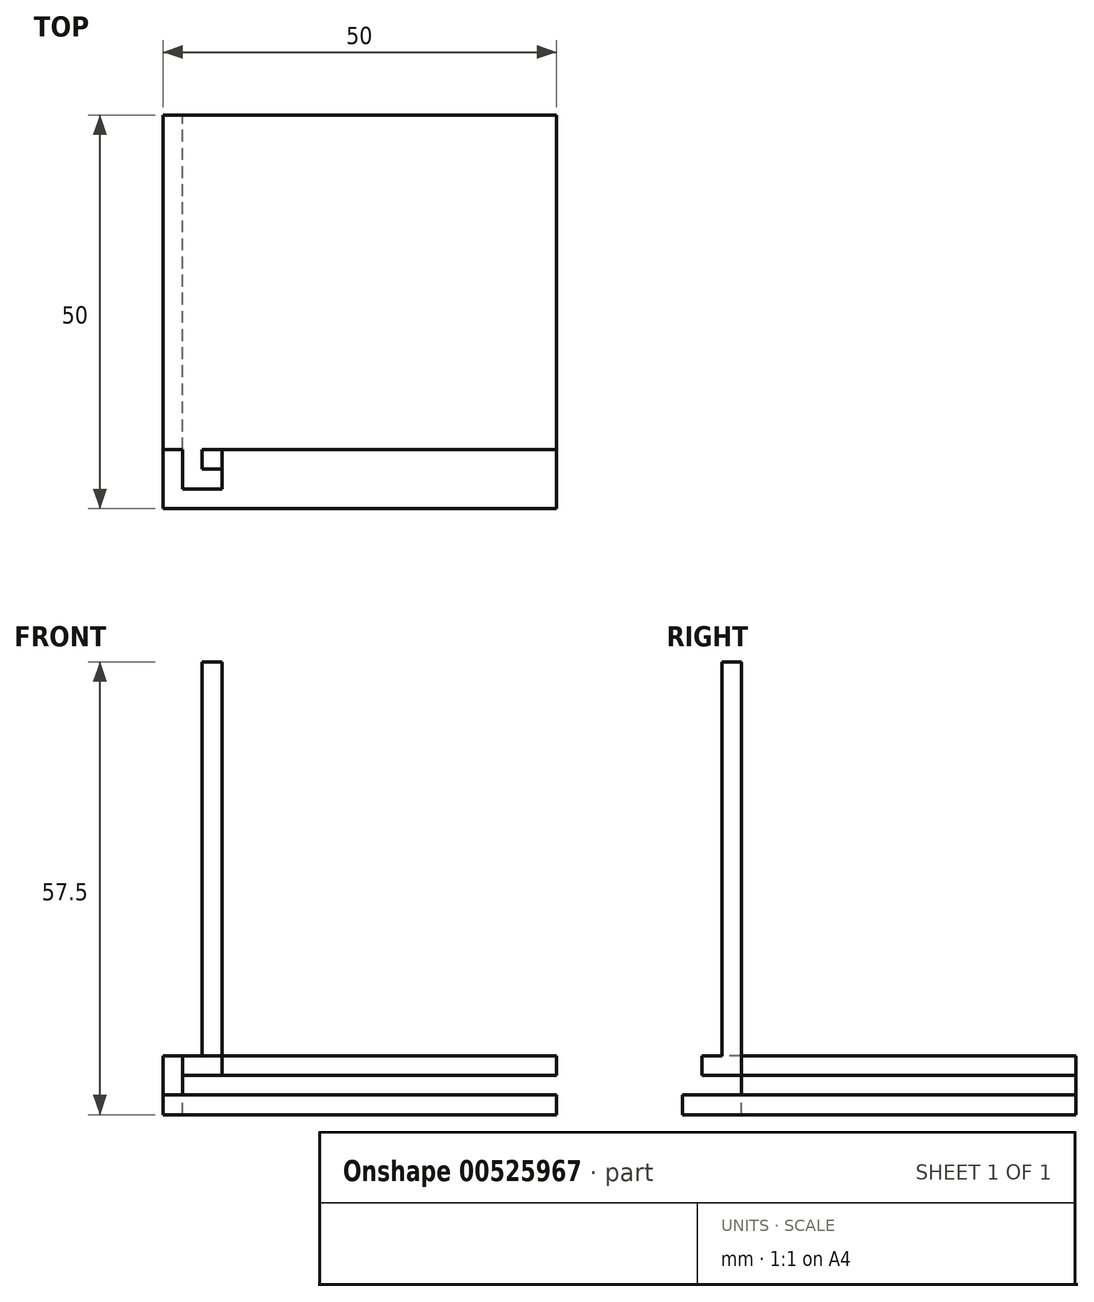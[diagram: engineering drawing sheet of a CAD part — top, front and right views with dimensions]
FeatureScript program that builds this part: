
annotation { "Feature Type Name" : "Feature", "Feature Type Description" : "" }
export const myFeature = defineFeature(function(context is Context, id is Id, definition is map)
    precondition{}
    {
        {
            var Q0;
            Q0=qCreatedBy(makeId("Top.planeOp"),FACE);
            var sketch = newSketch(context, id + "F0", { "sketchPlane" : qUnion([Q0])});
            skLineSegment(sketch, "E0.bottom", {"start": v(-21.7, 29.61) * mm, "end": v(28.3, 29.61) * mm});
            skLineSegment(sketch, "E0.top", {"start": v(-21.7, -20.39) * mm, "end": v(28.3, -20.39) * mm});
            skLineSegment(sketch, "E0.left", {"start": v(-21.7, 29.61) * mm, "end": v(-21.7, -20.39) * mm});
            skLineSegment(sketch, "E0.right", {"start": v(28.3, 29.61) * mm, "end": v(28.3, -20.39) * mm});
            skLineSegment(sketch, "E1.bottom", {"start": v(-21.7, 29.61) * mm, "end": v(-19.2, 29.61) * mm});
            skLineSegment(sketch, "E1.top", {"start": v(-21.7, -20.39) * mm, "end": v(-19.2, -20.39) * mm});
            skLineSegment(sketch, "E1.right", {"start": v(-19.2, 29.61) * mm, "end": v(-19.2, -20.39) * mm});
            skLineSegment(sketch, "E2.top", {"start": v(-21.7, -17.89) * mm, "end": v(28.3, -17.89) * mm});
            skLineSegment(sketch, "E2.left", {"start": v(-21.7, -20.39) * mm, "end": v(-21.7, -17.89) * mm});
            skLineSegment(sketch, "E2.right", {"start": v(28.3, -20.39) * mm, "end": v(28.3, -17.89) * mm});
            skLineSegment(sketch, "E3.bottom", {"start": v(-19.2, 29.61) * mm, "end": v(-16.7, 29.61) * mm});
            skLineSegment(sketch, "E3.top", {"start": v(-19.2, -20.39) * mm, "end": v(-16.7, -20.39) * mm});
            skLineSegment(sketch, "E3.right", {"start": v(-16.7, 29.61) * mm, "end": v(-16.7, -20.39) * mm});
            skLineSegment(sketch, "E4.bottom", {"start": v(-16.7, 29.61) * mm, "end": v(-14.2, 29.61) * mm});
            skLineSegment(sketch, "E4.top", {"start": v(-16.7, -20.39) * mm, "end": v(-14.2, -20.39) * mm});
            skLineSegment(sketch, "E4.right", {"start": v(-14.2, 29.61) * mm, "end": v(-14.2, -20.39) * mm});
            skLineSegment(sketch, "E5.top", {"start": v(-21.7, -15.39) * mm, "end": v(28.3, -15.39) * mm});
            skLineSegment(sketch, "E5.left", {"start": v(-21.7, -17.89) * mm, "end": v(-21.7, -15.39) * mm});
            skLineSegment(sketch, "E5.right", {"start": v(28.3, -17.89) * mm, "end": v(28.3, -15.39) * mm});
            skLineSegment(sketch, "E6.top", {"start": v(-21.7, -12.89) * mm, "end": v(28.3, -12.89) * mm});
            skLineSegment(sketch, "E6.left", {"start": v(-21.7, -15.39) * mm, "end": v(-21.7, -12.89) * mm});
            skLineSegment(sketch, "E6.right", {"start": v(28.3, -15.39) * mm, "end": v(28.3, -12.89) * mm});
            skSolve(sketch);
        }
        {
            var Q0;
            {var subQ0=sQuery(id+"F0.wireOp",EDGE,"E0.bottom");Q0=makeQuery(id+"F0.imprint","IMPRINT",FACE,{"disambiguationData":[TD([[makeQuery(id+"F0.imprint","IMPRINT",EDGE,{"derivedFrom":subQ0}),-1.0]])]});}
            var Q1;
            {var subQ0=sQuery(id+"F0.wireOp",EDGE,"E4.bottom");Q1=makeQuery(id+"F0.imprint","IMPRINT",FACE,{"disambiguationData":[TD([[makeQuery(id+"F0.imprint","IMPRINT",EDGE,{"derivedFrom":subQ0}),-1.0]])]});}
            var Q2;
            {var subQ0=sQuery(id+"F0.wireOp",EDGE,"E3.bottom");Q2=makeQuery(id+"F0.imprint","IMPRINT",FACE,{"disambiguationData":[TD([[makeQuery(id+"F0.imprint","IMPRINT",EDGE,{"derivedFrom":subQ0}),-1.0]])]});}
            var Q3;
            {var subQ0=sQuery(id+"F0.wireOp",EDGE,"E1.bottom");Q3=makeQuery(id+"F0.imprint","IMPRINT",FACE,{"disambiguationData":[TD([[makeQuery(id+"F0.imprint","IMPRINT",EDGE,{"derivedFrom":subQ0}),-1.0]])]});}
            var Q4;
            {var subQ5=sQuery(id+"F0.wireOp",EDGE,"E6.right");Q4=makeQuery(id+"F0.imprint","IMPRINT",FACE,{"disambiguationData":[TD([[makeQuery(id+"F0.imprint","IMPRINT",EDGE,{"derivedFrom":subQ5}),1.0]])]});}
            var Q5;
            {var subQ5=sQuery(id+"F0.wireOp",EDGE,"E5.right");Q5=makeQuery(id+"F0.imprint","IMPRINT",FACE,{"disambiguationData":[TD([[makeQuery(id+"F0.imprint","IMPRINT",EDGE,{"derivedFrom":subQ5}),1.0]])]});}
            var Q6;
            {var subQ0=sQuery(id+"F0.wireOp",EDGE,"E2.right");Q6=makeQuery(id+"F0.imprint","IMPRINT",FACE,{"disambiguationData":[TD([[makeQuery(id+"F0.imprint","IMPRINT",EDGE,{"derivedFrom":subQ0}),1.0]])]});}
            var Q7;
            {var subQ0=sQuery(id+"F0.wireOp",EDGE,"E4.top");Q7=makeQuery(id+"F0.imprint","IMPRINT",FACE,{"disambiguationData":[TD([[makeQuery(id+"F0.imprint","IMPRINT",EDGE,{"derivedFrom":subQ0}),1.0]])]});}
            var Q8;
            {var subQ0=sQuery(id+"F0.wireOp",EDGE,"E3.top");Q8=makeQuery(id+"F0.imprint","IMPRINT",FACE,{"disambiguationData":[TD([[makeQuery(id+"F0.imprint","IMPRINT",EDGE,{"derivedFrom":subQ0}),1.0]])]});}
            var Q9;
            {var subQ0=sQuery(id+"F0.wireOp",EDGE,"E2.left");Q9=makeQuery(id+"F0.imprint","IMPRINT",FACE,{"disambiguationData":[TD([[makeQuery(id+"F0.imprint","IMPRINT",EDGE,{"derivedFrom":subQ0}),-1.0]])]});}
            var Q10;
            {var subQ5=sQuery(id+"F0.wireOp",EDGE,"E5.left");Q10=makeQuery(id+"F0.imprint","IMPRINT",FACE,{"disambiguationData":[TD([[makeQuery(id+"F0.imprint","IMPRINT",EDGE,{"derivedFrom":subQ5}),-1.0]])]});}
            var Q11;
            {var subQ0=sQuery(id+"F0.wireOp",EDGE,"E5.top");var subQ1=sQuery(id+"F0.wireOp",EDGE,"E1.right");var subQ2=makeQuery(id+"F0.imprint","INTERSECT",VERTEX,{"derivedFrom":[subQ1,subQ0]});Q11=makeQuery(id+"F0.imprint","IMPRINT",FACE,{"disambiguationData":[TD([[makeQuery(id+"F0.imprint","IMPRINT",EDGE,{"disambiguationData":[TD([[subQ2,-1.0]])],"derivedFrom":subQ1}),1.0]])]});}
            var Q12;
            {var subQ0=sQuery(id+"F0.wireOp",EDGE,"E5.top");var subQ1=sQuery(id+"F0.wireOp",EDGE,"E3.right");var subQ2=makeQuery(id+"F0.imprint","INTERSECT",VERTEX,{"derivedFrom":[subQ1,subQ0]});Q12=makeQuery(id+"F0.imprint","IMPRINT",FACE,{"disambiguationData":[TD([[makeQuery(id+"F0.imprint","IMPRINT",EDGE,{"disambiguationData":[TD([[subQ2,-1.0]])],"derivedFrom":subQ1}),1.0]])]});}
            var Q13;
            {var subQ0=sQuery(id+"F0.wireOp",EDGE,"E6.top");var subQ1=sQuery(id+"F0.wireOp",EDGE,"E3.right");var subQ2=makeQuery(id+"F0.imprint","INTERSECT",VERTEX,{"derivedFrom":[subQ1,subQ0]});Q13=makeQuery(id+"F0.imprint","IMPRINT",FACE,{"disambiguationData":[TD([[makeQuery(id+"F0.imprint","IMPRINT",EDGE,{"disambiguationData":[TD([[subQ2,-1.0]])],"derivedFrom":subQ1}),1.0]])]});}
            var Q14;
            {var subQ0=sQuery(id+"F0.wireOp",EDGE,"E6.top");var subQ1=sQuery(id+"F0.wireOp",EDGE,"E1.right");var subQ2=makeQuery(id+"F0.imprint","INTERSECT",VERTEX,{"derivedFrom":[subQ1,subQ0]});Q14=makeQuery(id+"F0.imprint","IMPRINT",FACE,{"disambiguationData":[TD([[makeQuery(id+"F0.imprint","IMPRINT",EDGE,{"disambiguationData":[TD([[subQ2,-1.0]])],"derivedFrom":subQ1}),1.0]])]});}
            var Q15;
            {var subQ5=sQuery(id+"F0.wireOp",EDGE,"E6.left");Q15=makeQuery(id+"F0.imprint","IMPRINT",FACE,{"disambiguationData":[TD([[makeQuery(id+"F0.imprint","IMPRINT",EDGE,{"derivedFrom":subQ5}),-1.0]])]});}
            extrude(context, id + "F1", {"entities" : qUnion([Q0, Q1, Q2, Q3, Q4, Q5, Q6, Q7, Q8, Q9, Q10, Q11, Q12, Q13, Q14, Q15]), "oppositeDirection" : true, "depth" : 2.5 * mm, "offsetDistance" : 25 * mm});
        }
        {
            var Q0;
            {var subQ0=sQuery(id+"F0.wireOp",EDGE,"E1.bottom");Q0=makeQuery(id+"F0.imprint","IMPRINT",FACE,{"disambiguationData":[TD([[makeQuery(id+"F0.imprint","IMPRINT",EDGE,{"derivedFrom":subQ0}),-1.0]])]});}
            var Q1;
            {var subQ5=sQuery(id+"F0.wireOp",EDGE,"E6.left");Q1=makeQuery(id+"F0.imprint","IMPRINT",FACE,{"disambiguationData":[TD([[makeQuery(id+"F0.imprint","IMPRINT",EDGE,{"derivedFrom":subQ5}),-1.0]])]});}
            var Q2;
            {var subQ0=sQuery(id+"F0.wireOp",EDGE,"E4.bottom");Q2=makeQuery(id+"F0.imprint","IMPRINT",FACE,{"disambiguationData":[TD([[makeQuery(id+"F0.imprint","IMPRINT",EDGE,{"derivedFrom":subQ0}),-1.0]])]});}
            var Q3;
            {var subQ0=sQuery(id+"F0.wireOp",EDGE,"E6.top");var subQ1=sQuery(id+"F0.wireOp",EDGE,"E3.right");var subQ2=makeQuery(id+"F0.imprint","INTERSECT",VERTEX,{"derivedFrom":[subQ1,subQ0]});Q3=makeQuery(id+"F0.imprint","IMPRINT",FACE,{"disambiguationData":[TD([[makeQuery(id+"F0.imprint","IMPRINT",EDGE,{"disambiguationData":[TD([[subQ2,-1.0]])],"derivedFrom":subQ1}),1.0]])]});}
            var Q4;
            {var subQ0=sQuery(id+"F0.wireOp",EDGE,"E4.top");Q4=makeQuery(id+"F0.imprint","IMPRINT",FACE,{"disambiguationData":[TD([[makeQuery(id+"F0.imprint","IMPRINT",EDGE,{"derivedFrom":subQ0}),1.0]])]});}
            var Q5;
            {var subQ5=sQuery(id+"F0.wireOp",EDGE,"E6.right");Q5=makeQuery(id+"F0.imprint","IMPRINT",FACE,{"disambiguationData":[TD([[makeQuery(id+"F0.imprint","IMPRINT",EDGE,{"derivedFrom":subQ5}),1.0]])]});}
            var Q6;
            {var subQ0=sQuery(id+"F0.wireOp",EDGE,"E3.top");Q6=makeQuery(id+"F0.imprint","IMPRINT",FACE,{"disambiguationData":[TD([[makeQuery(id+"F0.imprint","IMPRINT",EDGE,{"derivedFrom":subQ0}),1.0]])]});}
            var Q7;
            {var subQ0=sQuery(id+"F0.wireOp",EDGE,"E2.left");Q7=makeQuery(id+"F0.imprint","IMPRINT",FACE,{"disambiguationData":[TD([[makeQuery(id+"F0.imprint","IMPRINT",EDGE,{"derivedFrom":subQ0}),-1.0]])]});}
            var Q8;
            {var subQ0=sQuery(id+"F0.wireOp",EDGE,"E2.right");Q8=makeQuery(id+"F0.imprint","IMPRINT",FACE,{"disambiguationData":[TD([[makeQuery(id+"F0.imprint","IMPRINT",EDGE,{"derivedFrom":subQ0}),1.0]])]});}
            var Q9;
            {var subQ5=sQuery(id+"F0.wireOp",EDGE,"E5.left");Q9=makeQuery(id+"F0.imprint","IMPRINT",FACE,{"disambiguationData":[TD([[makeQuery(id+"F0.imprint","IMPRINT",EDGE,{"derivedFrom":subQ5}),-1.0]])]});}
            extrude(context, id + "F2", {"entities" : qUnion([Q0, Q1, Q2, Q3, Q4, Q5, Q6, Q7, Q8, Q9]), "operationType" : NewBodyOperationType.ADD, "depth" : 50 * mm, "offsetDistance" : 25 * mm});
        }
        {
            var Q0;
            Q0=makeQuery(id+"F1.opExtrude","CAP_FACE",FACE,{"disambiguationData":[OSD([sQuery(id+"F0.wireOp",EDGE,"E0.bottom"),sQuery(id+"F0.wireOp",EDGE,"E0.right"),sQuery(id+"F0.wireOp",EDGE,"E1.bottom"),sQuery(id+"F0.wireOp",EDGE,"E0.left"),sQuery(id+"F0.wireOp",EDGE,"E0.top"),sQuery(id+"F0.wireOp",EDGE,"E2.left"),sQuery(id+"F0.wireOp",EDGE,"E2.right"),sQuery(id+"F0.wireOp",EDGE,"E3.bottom"),sQuery(id+"F0.wireOp",EDGE,"E3.top"),sQuery(id+"F0.wireOp",EDGE,"E4.bottom"),sQuery(id+"F0.wireOp",EDGE,"E4.top"),sQuery(id+"F0.wireOp",EDGE,"E5.left"),sQuery(id+"F0.wireOp",EDGE,"E5.right"),sQuery(id+"F0.wireOp",EDGE,"E6.left"),sQuery(id+"F0.wireOp",EDGE,"E6.right")])],"isStart":false});
            var sketch = newSketch(context, id + "F3", { "sketchPlane" : qUnion([Q0])});
            skLineSegment(sketch, "E7.bottom", {"start": v(-21.7, 20.39) * mm, "end": v(-19.2, 20.39) * mm});
            skLineSegment(sketch, "E7.top", {"start": v(-21.7, -29.61) * mm, "end": v(-19.2, -29.61) * mm});
            skLineSegment(sketch, "E7.left", {"start": v(-21.7, 20.39) * mm, "end": v(-21.7, -29.61) * mm});
            skLineSegment(sketch, "E7.right", {"start": v(-19.2, 20.39) * mm, "end": v(-19.2, -29.61) * mm});
            skLineSegment(sketch, "E8.bottom", {"start": v(-21.7, 20.39) * mm, "end": v(28.3, 20.39) * mm});
            skLineSegment(sketch, "E8.top", {"start": v(-21.7, 17.89) * mm, "end": v(28.3, 17.89) * mm});
            skLineSegment(sketch, "E8.left", {"start": v(-21.7, 20.39) * mm, "end": v(-21.7, 17.89) * mm});
            skLineSegment(sketch, "E8.right", {"start": v(28.3, 20.39) * mm, "end": v(28.3, 17.89) * mm});
            skSolve(sketch);
        }
        {
            var Q0;
            {var subQ0=sQuery(id+"F3.wireOp",EDGE,"E7.top");Q0=makeQuery(id+"F3.imprint","IMPRINT",FACE,{"disambiguationData":[TD([[makeQuery(id+"F3.imprint","IMPRINT",EDGE,{"derivedFrom":subQ0}),1.0]])]});}
            var Q1;
            {var subQ5=sQuery(id+"F3.wireOp",EDGE,"E8.right");Q1=makeQuery(id+"F3.imprint","IMPRINT",FACE,{"disambiguationData":[TD([[makeQuery(id+"F3.imprint","IMPRINT",EDGE,{"derivedFrom":subQ5}),1.0]])]});}
            var Q2;
            {var subQ5=sQuery(id+"F3.wireOp",EDGE,"E8.left");Q2=makeQuery(id+"F3.imprint","IMPRINT",FACE,{"disambiguationData":[TD([[makeQuery(id+"F3.imprint","IMPRINT",EDGE,{"derivedFrom":subQ5}),-1.0]])]});}
            extrude(context, id + "F4", {"entities" : qUnion([Q0, Q1, Q2]), "operationType" : NewBodyOperationType.ADD, "depth" : 2.5 * mm, "offsetDistance" : 25 * mm});
        }
        {
            var Q0;
            Q0=makeQuery(id+"F4.opExtrude","CAP_FACE",FACE,{"disambiguationData":[OSD([sQuery(id+"F3.wireOp",EDGE,"E7.top"),sQuery(id+"F3.wireOp",EDGE,"E7.left"),sQuery(id+"F3.wireOp",EDGE,"E7.right"),sQuery(id+"F3.wireOp",EDGE,"E8.bottom"),sQuery(id+"F3.wireOp",EDGE,"E8.top"),sQuery(id+"F3.wireOp",EDGE,"E8.left"),sQuery(id+"F3.wireOp",EDGE,"E8.right")])],"isStart":false});
            var sketch = newSketch(context, id + "F5", { "sketchPlane" : qUnion([Q0])});
            skLineSegment(sketch, "E9.bottom", {"start": v(-21.7, 20.39) * mm, "end": v(28.3, 20.39) * mm});
            skLineSegment(sketch, "E9.top", {"start": v(-21.7, -29.61) * mm, "end": v(28.3, -29.61) * mm});
            skLineSegment(sketch, "E9.left", {"start": v(-21.7, 20.39) * mm, "end": v(-21.7, -29.61) * mm});
            skLineSegment(sketch, "E9.right", {"start": v(28.3, 20.39) * mm, "end": v(28.3, -29.61) * mm});
            skSolve(sketch);
        }
        {
            var Q0;
            {var subQ1=makeQuery(id+"F4.opExtrude","CAP_EDGE",EDGE,{"disambiguationData":[OSD([sQuery(id+"F3.wireOp",EDGE,"E7.right")])],"isStart":false});Q0=makeQuery(id+"F5.imprint","IMPRINT",FACE,{"disambiguationData":[TD([[makeQuery(id+"F5.imprint","IMPRINT",EDGE,{"derivedFrom":subQ1}),1.0]])]});}
            var Q1;
            {var subQ4=sQuery(id+"F5.wireOp",EDGE,"E9.bottom");Q1=makeQuery(id+"F5.imprint","IMPRINT",FACE,{"disambiguationData":[TD([[makeQuery(id+"F5.imprint","IMPRINT",EDGE,{"derivedFrom":subQ4}),-1.0]])]});}
            extrude(context, id + "F6", {"entities" : qUnion([Q0, Q1]), "operationType" : NewBodyOperationType.ADD, "depth" : 2.5 * mm, "offsetDistance" : 25 * mm});
        }
    });
